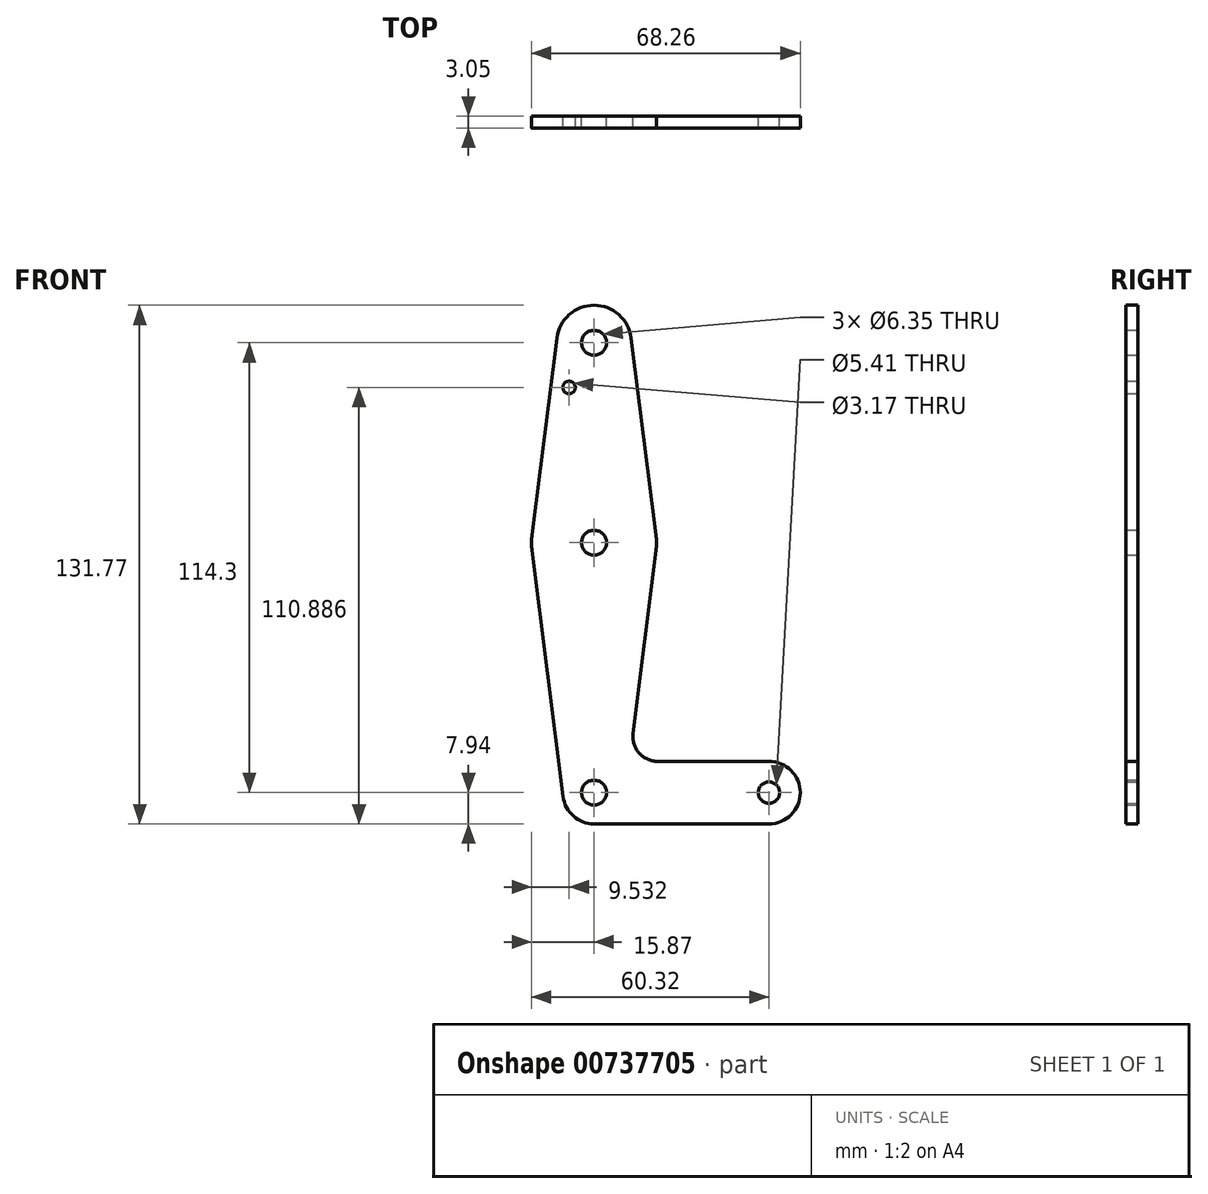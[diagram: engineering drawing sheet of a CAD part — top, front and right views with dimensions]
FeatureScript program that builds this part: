
annotation { "Feature Type Name" : "Feature", "Feature Type Description" : "" }
export const myFeature = defineFeature(function(context is Context, id is Id, definition is map)
    precondition{}
    {
        {
            var Q0;
            Q0=qCreatedBy(makeId("Front.planeOp"),FACE);
            var sketch = newSketch(context, id + "F0", { "sketchPlane" : qUnion([Q0])});
            skCircle(sketch, "E0", {"center": v(0, 114.3) * mm, "radius": 3.18 * mm});
            skCircle(sketch, "E1", {"center": v(0, 63.5) * mm, "radius": 3.18 * mm});
            skCircle(sketch, "E2", {"center": v(0, 0) * mm, "radius": 3.18 * mm});
            skCircle(sketch, "E3", {"center": v(44.45, 0) * mm, "radius": 2.7 * mm});
            skLineSegment(sketch, "E4", {"start": v(0, 0) * mm, "end": v(0, 114.3) * mm, "construction": true});
            skLineSegment(sketch, "E5", {"start": v(0, 0) * mm, "end": v(44.45, 0) * mm, "construction": true});
            skCircle(sketch, "E6", {"center": v(0, 114.3) * mm, "radius": 9.53 * mm});
            skCircle(sketch, "E7", {"center": v(0, 63.5) * mm, "radius": 15.88 * mm});
            skCircle(sketch, "E8", {"center": v(0, 0) * mm, "radius": 7.94 * mm});
            skCircle(sketch, "E9", {"center": v(44.45, 0) * mm, "radius": 7.94 * mm});
            skLineSegment(sketch, "E10", {"start": v(-9.45, 115.5) * mm, "end": v(-15.75, 65.48) * mm});
            skLineSegment(sketch, "E11", {"start": v(9.45, 115.5) * mm, "end": v(15.75, 65.48) * mm});
            skLineSegment(sketch, "E12", {"start": v(-15.75, 61.52) * mm, "end": v(-7.88, -1) * mm});
            skLineSegment(sketch, "E13", {"start": v(15.75, 61.52) * mm, "end": v(9.9, 15.08) * mm});
            skLineSegment(sketch, "E14", {"start": v(16.2, 7.94) * mm, "end": v(44.45, 7.94) * mm});
            skLineSegment(sketch, "E15", {"start": v(0, -7.94) * mm, "end": v(44.45, -7.94) * mm});
            skCircle(sketch, "E16", {"center": v(-6.34, 102.95) * mm, "radius": 1.59 * mm});
            skArc(sketch, "E17.filletArc", {"start": v(9.9, 15.08) * mm, "mid": v(11.44, 10.09) * mm, "end": v(16.2, 7.94) * mm});
            skSolve(sketch);
        }
        {
            var Q0;
            Q0 = qSketchRegion(id + "F0", true);
            extrude(context, id + "F1", {"entities" : qUnion([Q0]), "depth" : 3.05 * mm, "offsetDistance" : 25.4 * mm});
        }
    });
